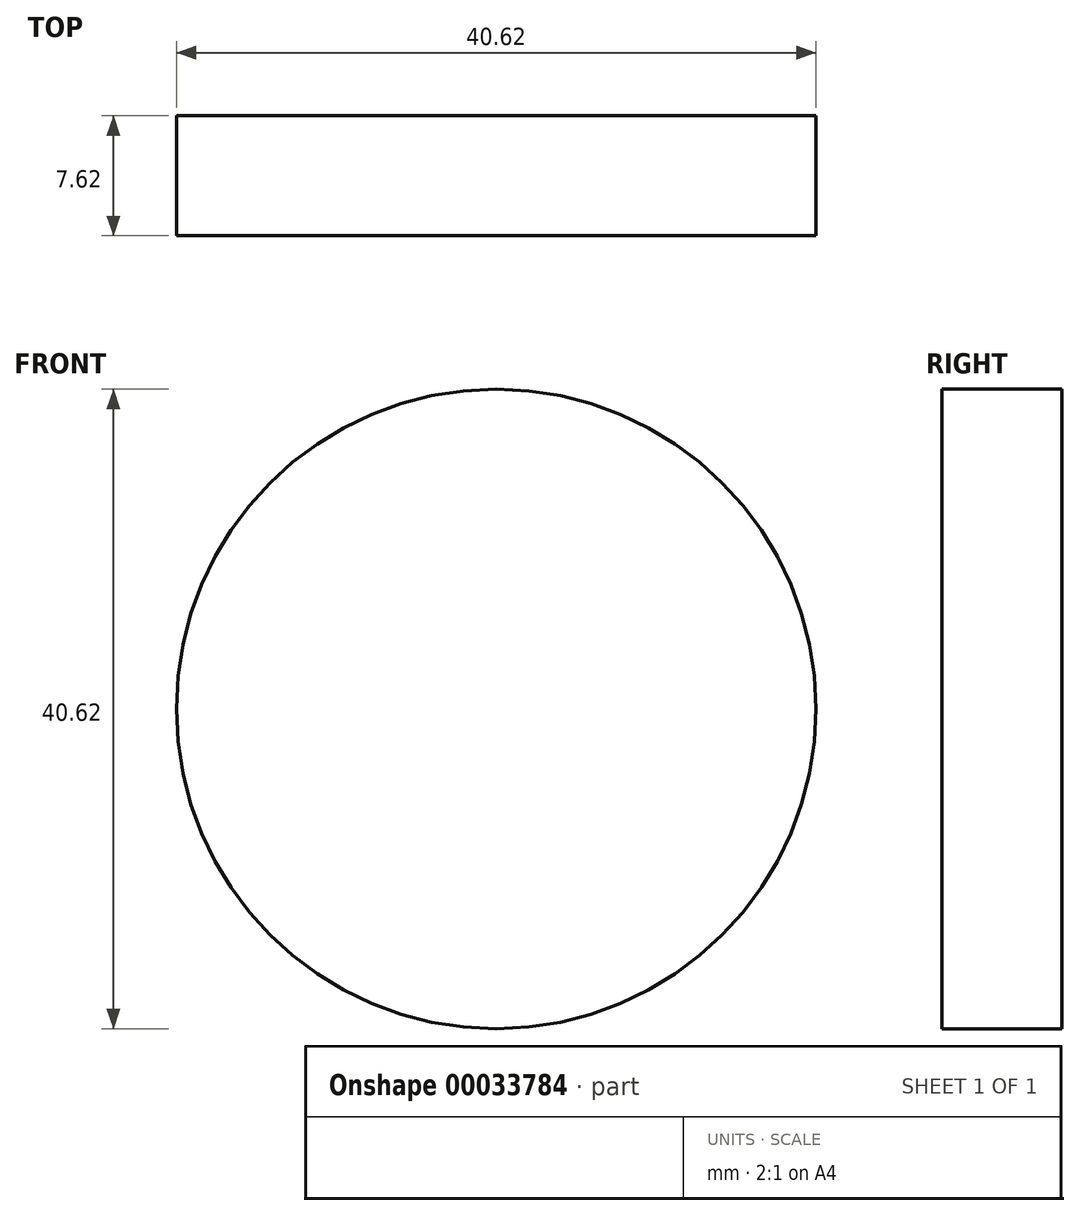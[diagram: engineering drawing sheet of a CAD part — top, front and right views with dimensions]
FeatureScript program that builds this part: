
annotation { "Feature Type Name" : "Feature", "Feature Type Description" : "" }
export const myFeature = defineFeature(function(context is Context, id is Id, definition is map)
    precondition{}
    {
        {
            var Q0;
            Q0=qCreatedBy(makeId("Front.planeOp"),FACE);
            var sketch = newSketch(context, id + "F0", { "sketchPlane" : qUnion([Q0])});
            skCircle(sketch, "E0", {"center": v(0, 0) * mm, "radius": 20.3 * mm});
            skSolve(sketch);
        }
        {
            var Q0;
            Q0=makeQuery(id+"F0.imprint","IMPRINT",FACE,{"disambiguationData":[TD([[makeQuery(id+"F0.imprint","IMPRINT",EDGE,{"derivedFrom":sQuery(id+"F0.wireOp",EDGE,"E0")}),1.0]])]});
            extrude(context, id + "F1", {"entities" : qUnion([Q0]), "depth" : 7.62 * mm});
        }
    });
